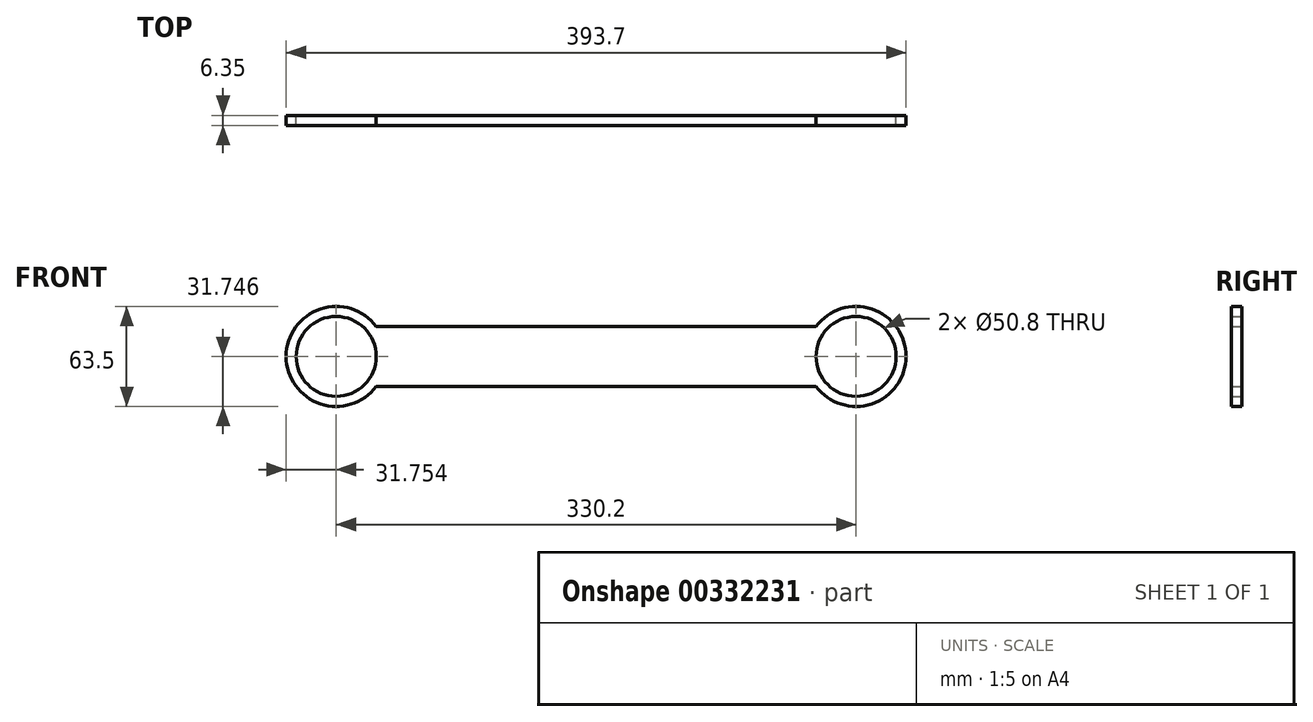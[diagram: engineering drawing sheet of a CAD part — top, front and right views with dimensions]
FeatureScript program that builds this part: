
annotation { "Feature Type Name" : "Feature", "Feature Type Description" : "" }
export const myFeature = defineFeature(function(context is Context, id is Id, definition is map)
    precondition{}
    {
        {
            var Q0;
            Q0=qCreatedBy(makeId("Front.planeOp"),FACE);
            var sketch = newSketch(context, id + "F0", { "sketchPlane" : qUnion([Q0])});
            skCircle(sketch, "E0", {"center": v(-68, 8.44) * mm, "radius": 25.4 * mm});
            skLineSegment(sketch, "E1", {"start": v(-42.6, 8.44) * mm, "end": v(236.8, 8.44) * mm, "construction": true});
            skLineSegment(sketch, "E2", {"start": v(236.8, 8.44) * mm, "end": v(262.2, 8.44) * mm, "construction": true});
            skCircle(sketch, "E3", {"center": v(262.2, 8.44) * mm, "radius": 25.4 * mm});
            skCircle(sketch, "E4", {"center": v(-68, 8.44) * mm, "radius": 31.75 * mm});
            skCircle(sketch, "E5", {"center": v(262.2, 8.44) * mm, "radius": 31.75 * mm});
            skLineSegment(sketch, "E6", {"start": v(97.1, 8.44) * mm, "end": v(97.1, 27.49) * mm, "construction": true});
            skLineSegment(sketch, "E7", {"start": v(97.1, 27.49) * mm, "end": v(236.8, 27.49) * mm});
            skLineSegment(sketch, "E8", {"start": v(236.8, 27.49) * mm, "end": v(-42.6, 27.49) * mm});
            skLineSegment(sketch, "E9.MirrorCS", {"start": v(236.8, -10.61) * mm, "end": v(-42.6, -10.61) * mm});
            skSolve(sketch);
        }
        {
            var Q0;
            Q0 = qSketchRegion(id + "F0", true);
            extrude(context, id + "F1", {"entities" : qUnion([Q0]), "depth" : 6.35 * mm});
        }
    });
